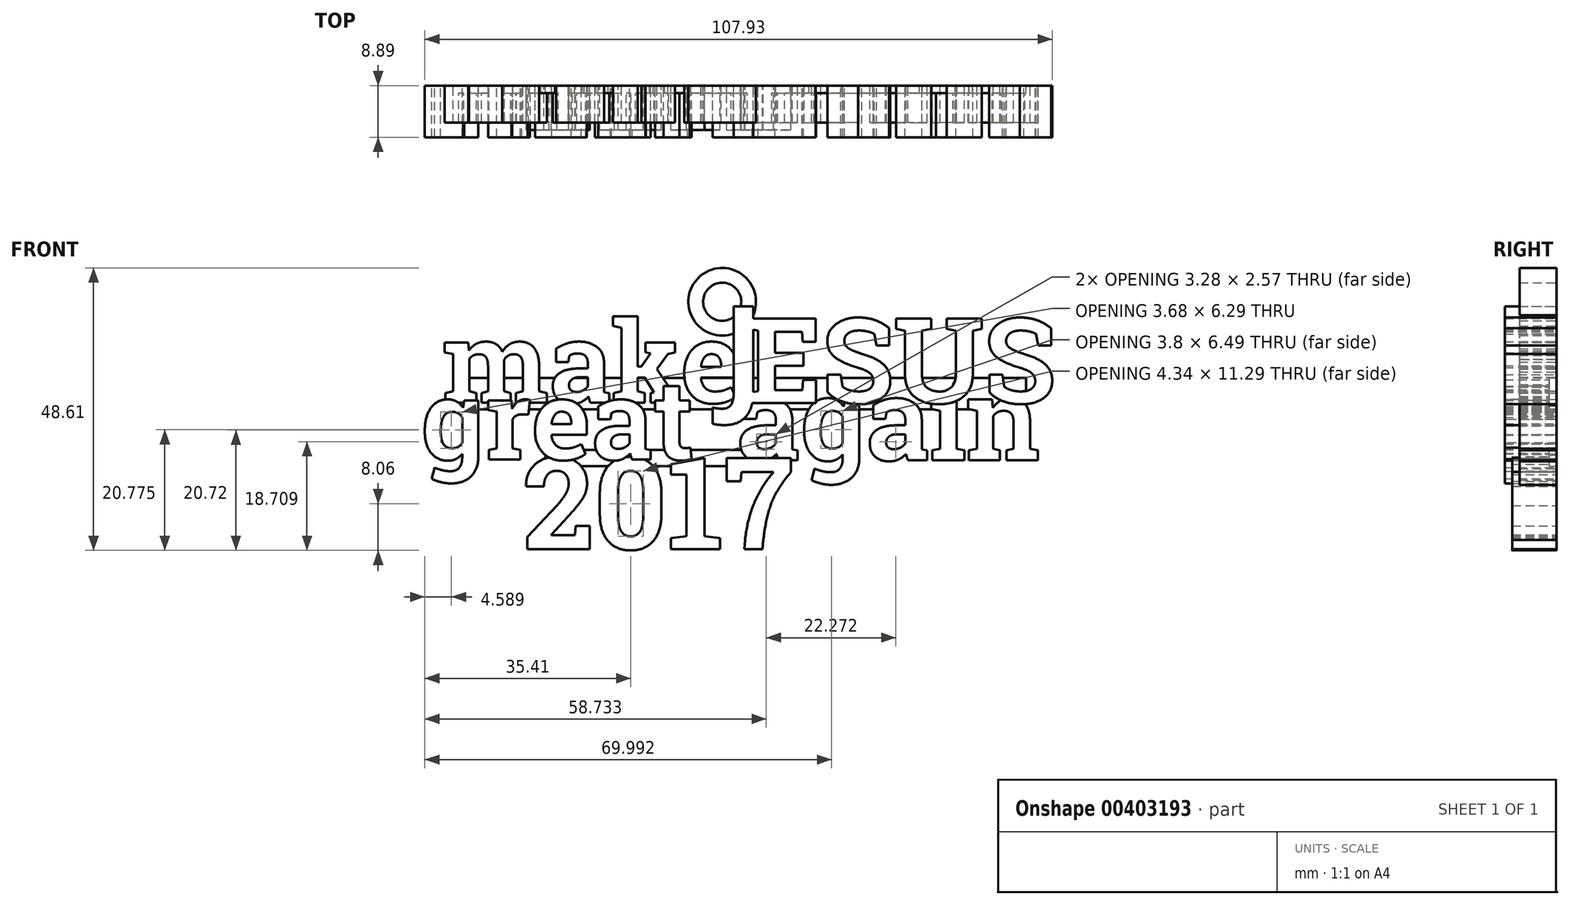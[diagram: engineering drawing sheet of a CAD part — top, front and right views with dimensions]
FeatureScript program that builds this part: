
annotation { "Feature Type Name" : "Feature", "Feature Type Description" : "" }
export const myFeature = defineFeature(function(context is Context, id is Id, definition is map)
    precondition{}
    {
        {
            var Q0;
            Q0=qCreatedBy(makeId("Front.planeOp"),FACE);
            cPlane(context, id + "F0", {"entities" : qUnion([Q0]), "cplaneType" : CPlaneType.OFFSET, "offset" : 6.35 * mm, "width" : 152.4 * mm, "height" : 152.4 * mm});
        }
        {
            var Q0;
            Q0=qCreatedBy(makeId("Front.planeOp"),FACE);
            var sketch = newSketch(context, id + "F1", { "sketchPlane" : qUnion([Q0])});
            skText(sketch, "E0", { "text": "make", "fontName": "RobotoSlab-Bold.ttf"});
            skText(sketch, "E1", { "text": "again", "fontName": "RobotoSlab-Bold.ttf"});
            const initialGuessF1  = {"E0": [-0.04805, -0.0025, 1, 0, 0.01409], "E1": [0.00239, -0.01238, 1, 0, 0.01431]};
            skSetInitialGuess(sketch, initialGuessF1);
            skSolve(sketch);
        }
        {
            var Q0;
            Q0 = qSketchRegion(id + "F1", true);
            var Q1;
            Q1=qCreatedBy(id+"F0.planeOp",FACE);
            extrude(context, id + "F2", {"entities" : qUnion([Q0]), "endBound" : BoundingType.UP_TO_SURFACE, "endBoundEntityFace" : qUnion([Q1]), "depth" : 25.4 * mm});
        }
        {
            var Q0;
            Q0=qCreatedBy(makeId("Front.planeOp"),FACE);
            var sketch = newSketch(context, id + "F3", { "sketchPlane" : qUnion([Q0])});
            skText(sketch, "E2", { "text": "ESUS", "fontName": "RobotoSlab-Bold.ttf"});
            skText(sketch, "E3", { "text": "J", "fontName": "OpenSans-Bold.ttf"});
            const initialGuessF3  = {"E2": [0.00406, -0.00255, 1, 0, 0.01472], "E3": [0, -0.0017, 1, 0, 0.0159]};
            skSetInitialGuess(sketch, initialGuessF3);
            skSolve(sketch);
        }
        {
            var Q0;
            Q0 = qSketchRegion(id + "F3", true);
            extrude(context, id + "F4", {"entities" : qUnion([Q0]), "operationType" : NewBodyOperationType.ADD, "depth" : 8.9 * mm});
        }
        {
            var Q0;
            Q0=qCreatedBy(makeId("Front.planeOp"),FACE);
            var sketch = newSketch(context, id + "F5", { "sketchPlane" : qUnion([Q0])});
            skText(sketch, "E4", { "text": "great", "fontName": "RobotoSlab-Bold.ttf"});
            const initialGuessF5  = {"E4": [-0.05192, -0.01227, 1, 0, 0.01386]};
            skSetInitialGuess(sketch, initialGuessF5);
            skSolve(sketch);
        }
        {
            var Q0;
            Q0 = qSketchRegion(id + "F5", true);
            extrude(context, id + "F6", {"entities" : qUnion([Q0]), "operationType" : NewBodyOperationType.ADD, "depth" : 8.9 * mm});
        }
        {
            var Q0;
            Q0=qCreatedBy(makeId("Front.planeOp"),FACE);
            var sketch = newSketch(context, id + "F7", { "sketchPlane" : qUnion([Q0])});
            skText(sketch, "E5", { "text": "2017", "fontName": "RobotoSlab-Bold.ttf"});
            const initialGuessF7  = {"E5": [-0.03428, -0.02768, 1, 0, 0.01587]};
            skSetInitialGuess(sketch, initialGuessF7);
            skSolve(sketch);
        }
        {
            var Q0;
            Q0 = qSketchRegion(id + "F7", true);
            extrude(context, id + "F8", {"entities" : qUnion([Q0]), "operationType" : NewBodyOperationType.ADD, "depth" : 7.62 * mm});
        }
        {
            var Q0;
            Q0=qCreatedBy(makeId("Front.planeOp"),FACE);
            var sketch = newSketch(context, id + "F9", { "sketchPlane" : qUnion([Q0])});
            skCircle(sketch, "E6", {"center": v(0, 14.88) * mm, "radius": 5.82 * mm});
            skCircle(sketch, "E7", {"center": v(0, 14.88) * mm, "radius": 3.28 * mm});
            skSolve(sketch);
        }
        {
            var Q0;
            Q0 = qSketchRegion(id + "F9", true);
            extrude(context, id + "F10", {"entities" : qUnion([Q0]), "operationType" : NewBodyOperationType.ADD, "depth" : 6.35 * mm});
        }
        {
            var Q0;
            Q0=qCreatedBy(makeId("Front.planeOp"),FACE);
            var sketch = newSketch(context, id + "F11", { "sketchPlane" : qUnion([Q0])});
            skCircle(sketch, "E8", {"center": v(37.43, 2.14) * mm, "radius": 2.72 * mm});
            skSolve(sketch);
        }
        {
            var Q0;
            Q0 = qSketchRegion(id + "F11", true);
            extrude(context, id + "F12", {"entities" : qUnion([Q0]), "operationType" : NewBodyOperationType.REMOVE, "endBound" : BoundingType.THROUGH_ALL, "depth" : 25.4 * mm});
        }
        {
            var Q0;
            Q0=qCreatedBy(makeId("Front.planeOp"),FACE);
            var sketch = newSketch(context, id + "F13", { "sketchPlane" : qUnion([Q0])});
            skLineSegment(sketch, "E9.bottom", {"start": v(-45.86, 1.77) * mm, "end": v(52.26, 1.77) * mm});
            skLineSegment(sketch, "E9.top", {"start": v(-45.86, -3.62) * mm, "end": v(52.26, -3.62) * mm});
            skLineSegment(sketch, "E9.left", {"start": v(-45.86, 1.77) * mm, "end": v(-45.86, -3.62) * mm});
            skLineSegment(sketch, "E9.right", {"start": v(52.26, 1.77) * mm, "end": v(52.26, -3.62) * mm});
            skLineSegment(sketch, "E10.bottom", {"start": v(-30.38, -10.6) * mm, "end": v(10.88, -10.6) * mm});
            skLineSegment(sketch, "E10.top", {"start": v(-30.38, -13.41) * mm, "end": v(10.88, -13.41) * mm});
            skLineSegment(sketch, "E10.left", {"start": v(-30.38, -10.6) * mm, "end": v(-30.38, -13.41) * mm});
            skLineSegment(sketch, "E10.right", {"start": v(10.88, -10.6) * mm, "end": v(10.88, -13.41) * mm});
            skSolve(sketch);
        }
        {
            var Q0;
            Q0 = qSketchRegion(id + "F13", true);
            extrude(context, id + "F14", {"entities" : qUnion([Q0]), "operationType" : NewBodyOperationType.ADD, "depth" : 1.27 * mm});
        }
    });
